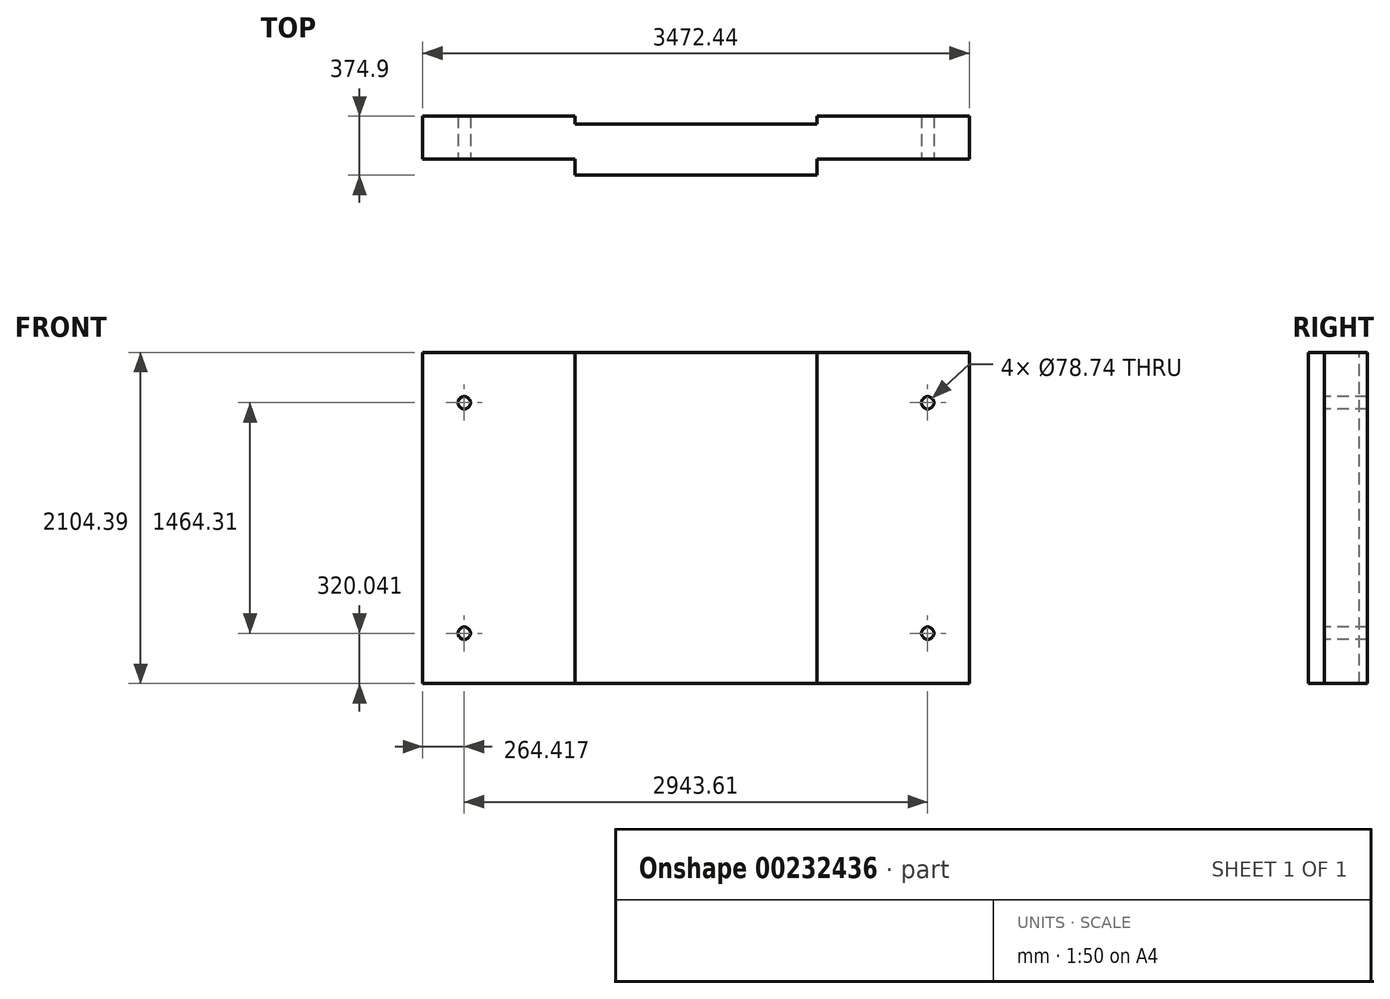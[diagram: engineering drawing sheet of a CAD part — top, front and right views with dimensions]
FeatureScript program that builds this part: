
annotation { "Feature Type Name" : "Feature", "Feature Type Description" : "" }
export const myFeature = defineFeature(function(context is Context, id is Id, definition is map)
    precondition{}
    {
        {
            var Q0;
            Q0=qCreatedBy(makeId("Front.planeOp"),FACE);
            var sketch = newSketch(context, id + "F0", { "sketchPlane" : qUnion([Q0])});
            skLineSegment(sketch, "E0.bottom", {"start": v(-1720.53, 1169) * mm, "end": v(1751.9, 1169) * mm});
            skLineSegment(sketch, "E0.top", {"start": v(-1720.53, -935.4) * mm, "end": v(1751.9, -935.4) * mm});
            skLineSegment(sketch, "E0.left", {"start": v(-1720.53, 1169) * mm, "end": v(-1720.53, -935.4) * mm});
            skLineSegment(sketch, "E0.right", {"start": v(1751.9, 1169) * mm, "end": v(1751.9, -935.4) * mm});
            skSolve(sketch);
        }
        {
            var Q0;
            Q0 = qSketchRegion(id + "F0", true);
            extrude(context, id + "F1", {"entities" : qUnion([Q0]), "depth" : 272.03 * mm});
        }
        {
            var Q0;
            Q0=makeQuery(id+"F1.opExtrude","CAP_FACE",FACE,{"disambiguationData":[OSD([sQuery(id+"F0.wireOp",EDGE,"E0.bottom"),sQuery(id+"F0.wireOp",EDGE,"E0.top"),sQuery(id+"F0.wireOp",EDGE,"E0.left"),sQuery(id+"F0.wireOp",EDGE,"E0.right")])],"isStart":false});
            var sketch = newSketch(context, id + "F2", { "sketchPlane" : qUnion([Q0])});
            skLineSegment(sketch, "E1", {"start": v(-1720.53, -935.4) * mm, "end": v(-753.55, -935.4) * mm, "construction": true});
            skLineSegment(sketch, "E2", {"start": v(1751.9, -935.4) * mm, "end": v(784.93, -935.4) * mm, "construction": true});
            skLineSegment(sketch, "E3", {"start": v(-753.55, -935.4) * mm, "end": v(-753.55, 1169) * mm});
            skLineSegment(sketch, "E4", {"start": v(784.93, -935.4) * mm, "end": v(784.93, 1169) * mm});
            skLineSegment(sketch, "E5", {"start": v(784.93, 1169) * mm, "end": v(-753.55, 1169) * mm});
            skLineSegment(sketch, "E6", {"start": v(-753.55, -935.4) * mm, "end": v(784.93, -935.4) * mm});
            skSolve(sketch);
        }
        {
            var Q0;
            Q0=makeQuery(id+"F2.imprint","IMPRINT",FACE,{"disambiguationData":[TD([[makeQuery(id+"F2.imprint","IMPRINT",EDGE,{"derivedFrom":sQuery(id+"F2.wireOp",EDGE,"E3")}),-1.0]])]});
            extrude(context, id + "F3", {"entities" : qUnion([Q0]), "operationType" : NewBodyOperationType.ADD, "depth" : 102.87 * mm});
        }
        {
            var Q0;
            Q0=makeQuery(id+"F3.boolean.opBoolean","MERGE",FACE,{"derivedFrom":[makeQuery(id+"F1.opExtrude","SWEPT_FACE",FACE,{"disambiguationData":[OSD([sQuery(id+"F0.wireOp",EDGE,"E0.bottom")])]}),makeQuery(id+"F3.opExtrude","SWEPT_FACE",FACE,{"disambiguationData":[OSD([sQuery(id+"F2.wireOp",EDGE,"E5")])]})]});
            var sketch = newSketch(context, id + "F4", { "sketchPlane" : qUnion([Q0])});
            skLineSegment(sketch, "E7", {"start": v(-753.55, 0) * mm, "end": v(-753.55, -51.3) * mm});
            skLineSegment(sketch, "E8", {"start": v(784.93, 0) * mm, "end": v(784.93, -51.3) * mm});
            skLineSegment(sketch, "E9", {"start": v(-753.55, -51.3) * mm, "end": v(784.93, -51.3) * mm});
            skSolve(sketch);
        }
        {
            var Q0;
            {var subQ0=sQuery(id+"F4.wireOp",EDGE,"E7");Q0=makeQuery(id+"F4.imprint","IMPRINT",FACE,{"disambiguationData":[TD([[makeQuery(id+"F4.imprint","IMPRINT",EDGE,{"derivedFrom":subQ0}),1.0]])]});}
            extrude(context, id + "F5", {"entities" : qUnion([Q0]), "operationType" : NewBodyOperationType.REMOVE, "endBound" : BoundingType.THROUGH_ALL, "oppositeDirection" : true, "depth" : 25.4 * mm});
        }
        {
            var Q0;
            {var subQ0=sQuery(id+"F0.wireOp",EDGE,"E0.left");var subQ1=sQuery(id+"F0.wireOp",EDGE,"E0.top");var subQ2=sQuery(id+"F0.wireOp",EDGE,"E0.bottom");Q0=makeQuery(id+"F3.boolean.opBoolean","SPLIT",FACE,{"disambiguationData":[TD([makeQuery(id+"F1.opExtrude","SWEPT_FACE",FACE,{"disambiguationData":[OSD([subQ0])]})])],"derivedFrom":makeQuery(id+"F1.opExtrude","CAP_FACE",FACE,{"disambiguationData":[OSD([subQ2,subQ1,subQ0,sQuery(id+"F0.wireOp",EDGE,"E0.right")])],"isStart":false})});}
            var sketch = newSketch(context, id + "F6", { "sketchPlane" : qUnion([Q0])});
            skCircle(sketch, "E10", {"center": v(-1456.11, 848.95) * mm, "radius": 39.37 * mm});
            skCircle(sketch, "E11", {"center": v(-1456.11, -615.36) * mm, "radius": 39.37 * mm});
            skCircle(sketch, "E12", {"center": v(1487.5, 848.95) * mm, "radius": 39.37 * mm});
            skCircle(sketch, "E13", {"center": v(1487.5, -615.36) * mm, "radius": 39.37 * mm});
            skSolve(sketch);
        }
        {
            var Q0;
            Q0=makeQuery(id+"F6.imprint","IMPRINT",FACE,{"disambiguationData":[TD([[makeQuery(id+"F6.imprint","IMPRINT",EDGE,{"derivedFrom":sQuery(id+"F6.wireOp",EDGE,"E10")}),1.0]])]});
            var Q1;
            Q1=makeQuery(id+"F6.imprint","IMPRINT",FACE,{"disambiguationData":[TD([[makeQuery(id+"F6.imprint","IMPRINT",EDGE,{"derivedFrom":sQuery(id+"F6.wireOp",EDGE,"E11")}),1.0]])]});
            var Q2;
            Q2=makeQuery(id+"F6.imprint","IMPRINT",FACE,{"disambiguationData":[TD([[makeQuery(id+"F6.imprint","IMPRINT",EDGE,{"derivedFrom":sQuery(id+"F6.wireOp",EDGE,"E12")}),1.0]])]});
            var Q3;
            Q3=makeQuery(id+"F6.imprint","IMPRINT",FACE,{"disambiguationData":[TD([[makeQuery(id+"F6.imprint","IMPRINT",EDGE,{"derivedFrom":sQuery(id+"F6.wireOp",EDGE,"E13")}),1.0]])]});
            extrude(context, id + "F7", {"entities" : qUnion([Q0, Q1, Q2, Q3]), "operationType" : NewBodyOperationType.REMOVE, "endBound" : BoundingType.THROUGH_ALL, "oppositeDirection" : true, "depth" : 25.4 * mm});
        }
    });
